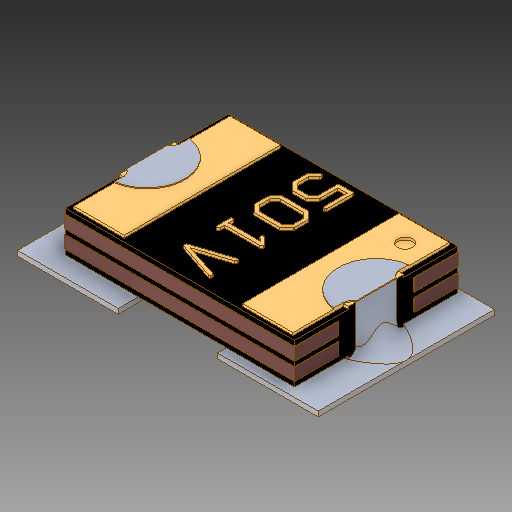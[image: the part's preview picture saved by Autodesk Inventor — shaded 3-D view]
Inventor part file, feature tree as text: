
AUTODESK INVENTOR PART (.ipt)
format: ipt  version: 2019.4 (Build 234330000, 330)  size: 544,256 bytes
history: native  units: in
note: dims shown in document units (in); Inventor stores cm internally (conversion verified against a paired STEP export)
features: mirror x1
ambient origin geometry x8: Origin, YZ Plane, XZ Plane, XY Plane, X Axis, Y Axis, Z Axis, Center Point
bodies: Solid1 (feature_tree)
feature tree (1):
  mirror  "Mirror5"
